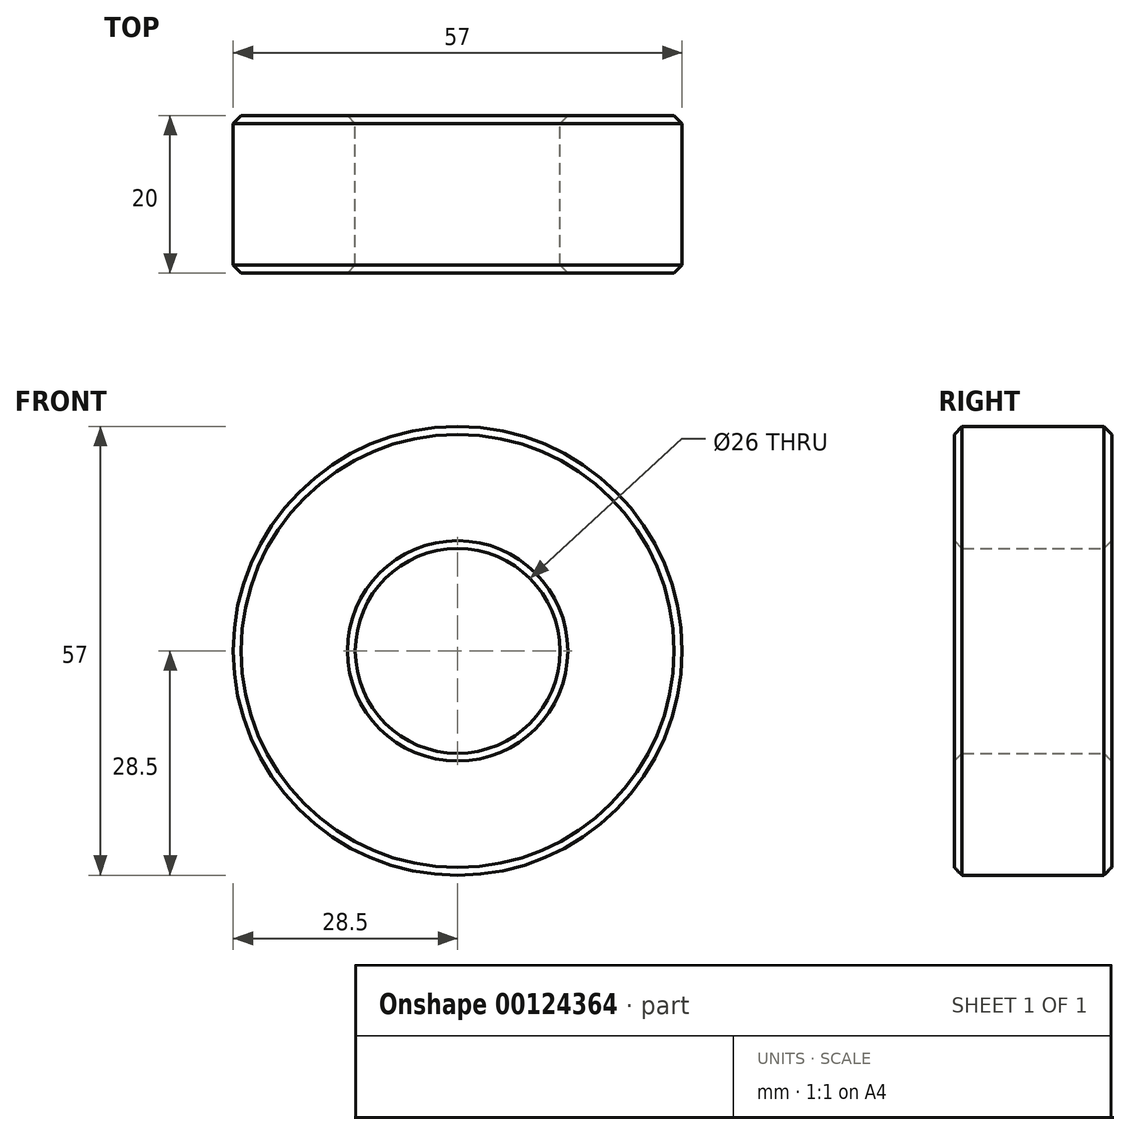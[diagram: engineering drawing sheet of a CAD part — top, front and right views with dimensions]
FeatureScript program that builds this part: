
annotation { "Feature Type Name" : "Feature", "Feature Type Description" : "" }
export const myFeature = defineFeature(function(context is Context, id is Id, definition is map)
    precondition{}
    {
        {
            var Q0;
            Q0=qCreatedBy(makeId("Front.planeOp"),FACE);
            var sketch = newSketch(context, id + "F0", { "sketchPlane" : qUnion([Q0])});
            skCircle(sketch, "E0", {"center": v(0, 0) * mm, "radius": 13 * mm});
            skCircle(sketch, "E1", {"center": v(0, 0) * mm, "radius": 28.5 * mm});
            skSolve(sketch);
        }
        {
            var Q0;
            Q0=makeQuery(id+"F0.imprint","IMPRINT",FACE,{"disambiguationData":[TD([[makeQuery(id+"F0.imprint","IMPRINT",EDGE,{"derivedFrom":sQuery(id+"F0.wireOp",EDGE,"E0")}),-1.0]])]});
            extrude(context, id + "F1", {"entities" : qUnion([Q0]), "depth" : 20 * mm});
        }
        {
            var Q0;
            Q0=makeQuery(id+"F1.opExtrude","CAP_FACE",FACE,{"disambiguationData":[OSD([sQuery(id+"F0.wireOp",EDGE,"E0"),sQuery(id+"F0.wireOp",EDGE,"E1")])],"isStart":false});
            var Q1;
            Q1=makeQuery(id+"F1.opExtrude","CAP_FACE",FACE,{"disambiguationData":[OSD([sQuery(id+"F0.wireOp",EDGE,"E0"),sQuery(id+"F0.wireOp",EDGE,"E1")])],"isStart":true});
            chamfer(context, id + "F2", {"entities" : qUnion([Q0, Q1]), "width" : 1 * mm, "tangentPropagation" : true});
        }
    });
